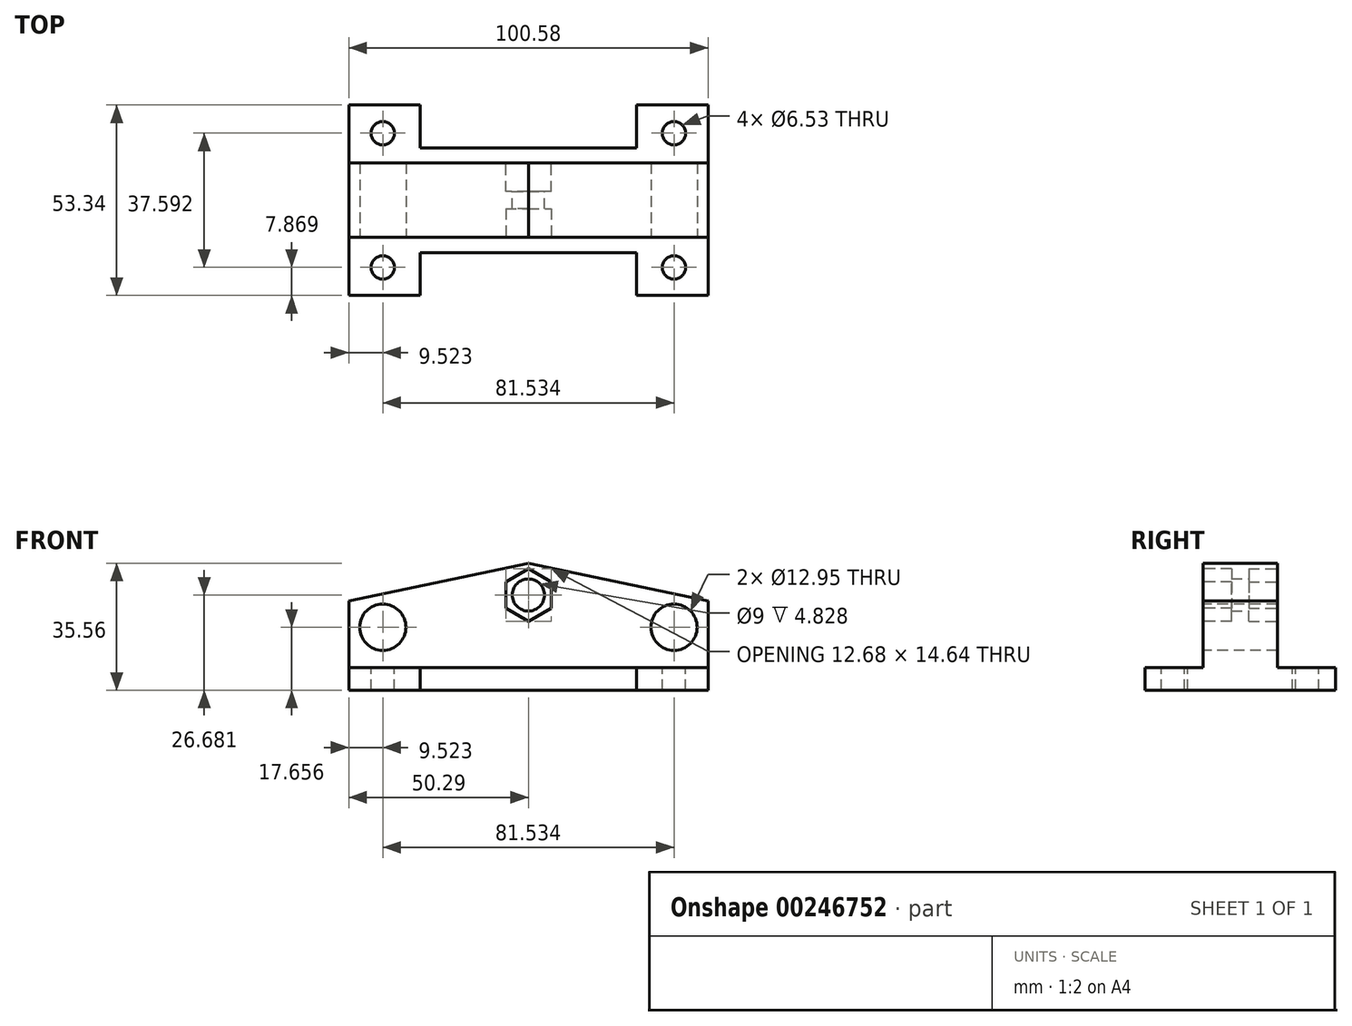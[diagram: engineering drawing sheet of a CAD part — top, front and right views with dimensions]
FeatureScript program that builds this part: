
annotation { "Feature Type Name" : "Feature", "Feature Type Description" : "" }
export const myFeature = defineFeature(function(context is Context, id is Id, definition is map)
    precondition{}
    {
        {
            var Q0;
            Q0=qCreatedBy(makeId("Top.planeOp"),FACE);
            var sketch = newSketch(context, id + "F0", { "sketchPlane" : qUnion([Q0])});
            skLineSegment(sketch, "E0.bottom", {"start": v(-48.14, 27.76) * mm, "end": v(52.44, 27.76) * mm});
            skLineSegment(sketch, "E0.top", {"start": v(-48.14, -25.58) * mm, "end": v(52.44, -25.58) * mm});
            skLineSegment(sketch, "E0.left", {"start": v(-48.14, 27.76) * mm, "end": v(-48.14, -25.58) * mm});
            skLineSegment(sketch, "E0.right", {"start": v(52.44, 27.76) * mm, "end": v(52.44, -25.58) * mm});
            skSolve(sketch);
        }
        {
            var Q0;
            Q0 = qSketchRegion(id + "F0", true);
            extrude(context, id + "F1", {"entities" : qUnion([Q0]), "depth" : 6.35 * mm});
        }
        {
            var Q0;
            Q0=makeQuery(id+"F1.opExtrude","CAP_FACE",FACE,{"disambiguationData":[OSD([sQuery(id+"F0.wireOp",EDGE,"E0.bottom"),sQuery(id+"F0.wireOp",EDGE,"E0.top"),sQuery(id+"F0.wireOp",EDGE,"E0.left"),sQuery(id+"F0.wireOp",EDGE,"E0.right")])],"isStart":false});
            var sketch = newSketch(context, id + "F2", { "sketchPlane" : qUnion([Q0])});
            skLineSegment(sketch, "E1.bottom", {"start": v(-48.14, 11.5) * mm, "end": v(52.44, 11.5) * mm});
            skLineSegment(sketch, "E1.top", {"start": v(-48.14, -9.33) * mm, "end": v(52.44, -9.33) * mm});
            skLineSegment(sketch, "E1.left", {"start": v(-48.14, 11.5) * mm, "end": v(-48.14, -9.33) * mm});
            skLineSegment(sketch, "E1.right", {"start": v(52.44, 11.5) * mm, "end": v(52.44, -9.33) * mm});
            skSolve(sketch);
        }
        {
            var Q0;
            Q0 = qSketchRegion(id + "F2", true);
            extrude(context, id + "F3", {"entities" : qUnion([Q0]), "operationType" : NewBodyOperationType.ADD, "depth" : 29.21 * mm});
        }
        {
            var Q0;
            Q0=makeQuery(id+"F3.opExtrude","SWEPT_FACE",FACE,{"disambiguationData":[OSD([sQuery(id+"F2.wireOp",EDGE,"E1.top")])]});
            var sketch = newSketch(context, id + "F4", { "sketchPlane" : qUnion([Q0])});
            skCircle(sketch, "E2.cCircle", {"center": v(2.15, 26.68) * mm, "radius": 6.34 * mm, "construction": true});
            skLineSegment(sketch, "E2.0", {"start": v(8.49, 30.34) * mm, "end": v(8.49, 23.02) * mm});
            skLineSegment(sketch, "E2.1", {"start": v(8.49, 23.02) * mm, "end": v(2.15, 19.36) * mm});
            skLineSegment(sketch, "E2.2", {"start": v(2.15, 19.36) * mm, "end": v(-4.2, 23.02) * mm});
            skLineSegment(sketch, "E2.3", {"start": v(-4.2, 23.02) * mm, "end": v(-4.2, 30.34) * mm});
            skLineSegment(sketch, "E2.4", {"start": v(-4.2, 30.34) * mm, "end": v(2.15, 34) * mm});
            skLineSegment(sketch, "E2.5", {"start": v(2.15, 34) * mm, "end": v(8.49, 30.34) * mm});
            skPoint(sketch, "E2.0.midPoint", {"position": v(8.49, 26.68) * mm});
            skSolve(sketch);
        }
        {
            var Q0;
            Q0 = qSketchRegion(id + "F4", true);
            extrude(context, id + "F5", {"entities" : qUnion([Q0]), "operationType" : NewBodyOperationType.REMOVE, "oppositeDirection" : true, "depth" : 8 * mm});
        }
        {
            var Q0;
            Q0=makeQuery(id+"F3.opExtrude","SWEPT_FACE",FACE,{"disambiguationData":[OSD([sQuery(id+"F2.wireOp",EDGE,"E1.bottom")])]});
            var sketch = newSketch(context, id + "F6", { "sketchPlane" : qUnion([Q0])});
            skCircle(sketch, "E3.cCircle", {"center": v(-2.15, 26.68) * mm, "radius": 6.34 * mm, "construction": true});
            skLineSegment(sketch, "E3.0", {"start": v(4.2, 30.34) * mm, "end": v(4.2, 23.02) * mm});
            skLineSegment(sketch, "E3.1", {"start": v(4.2, 23.02) * mm, "end": v(-2.15, 19.36) * mm});
            skLineSegment(sketch, "E3.2", {"start": v(-2.15, 19.36) * mm, "end": v(-8.49, 23.02) * mm});
            skLineSegment(sketch, "E3.3", {"start": v(-8.49, 23.02) * mm, "end": v(-8.49, 30.34) * mm});
            skLineSegment(sketch, "E3.4", {"start": v(-8.49, 30.34) * mm, "end": v(-2.15, 34) * mm});
            skLineSegment(sketch, "E3.5", {"start": v(-2.15, 34) * mm, "end": v(4.2, 30.34) * mm});
            skPoint(sketch, "E3.0.midPoint", {"position": v(4.2, 26.68) * mm});
            skSolve(sketch);
        }
        {
            var Q0;
            Q0 = qSketchRegion(id + "F6", true);
            extrude(context, id + "F7", {"entities" : qUnion([Q0]), "operationType" : NewBodyOperationType.REMOVE, "oppositeDirection" : true, "depth" : 8 * mm});
        }
        {
            var Q0;
            Q0=makeQuery(id+"F3.opExtrude","SWEPT_FACE",FACE,{"disambiguationData":[OSD([sQuery(id+"F2.wireOp",EDGE,"E1.bottom")])]});
            var sketch = newSketch(context, id + "F8", { "sketchPlane" : qUnion([Q0])});
            skPoint(sketch, "E4", {"position": v(-2.15, 26.68) * mm});
            skPoint(sketch, "E4.positionSnap0", {"position": v(4.2, 26.68) * mm});
            skSolve(sketch);
        }
        {
            var Q0;
            Q0=sQuery(id+"F8.wireOp",VERTEX,"E4");
            var Q1;
            Q1=makeQuery(id+"F1.opExtrude","SWEPT_BODY",BODY,{"disambiguationData":[OSD([sQuery(id+"F0.wireOp",EDGE,"E0.bottom"),sQuery(id+"F0.wireOp",EDGE,"E0.top"),sQuery(id+"F0.wireOp",EDGE,"E0.left"),sQuery(id+"F0.wireOp",EDGE,"E0.right")])]});
            hole(context, id + "F9", {"style" : HoleStyle.SIMPLE, "endStyle" : HoleEndStyle.THROUGH, "holeDiameter" : 9 * mm, "tappedDepth" : 12 * mm, "tapClearance" : 3, "locations" : qUnion([Q0]), "scope" : qUnion([Q1])});
        }
        {
            var Q0;
            Q0=makeQuery(id+"F3.opExtrude","SWEPT_FACE",FACE,{"disambiguationData":[OSD([sQuery(id+"F2.wireOp",EDGE,"E1.top")])]});
            var sketch = newSketch(context, id + "F10", { "sketchPlane" : qUnion([Q0])});
            skPoint(sketch, "E5", {"position": v(-38.62, 17.66) * mm});
            skPoint(sketch, "E6", {"position": v(42.92, 17.66) * mm});
            skSolve(sketch);
        }
        {
            var Q0;
            Q0=sQuery(id+"F10.wireOp",VERTEX,"E6");
            var Q1;
            Q1=sQuery(id+"F10.wireOp",VERTEX,"E5");
            var Q2;
            Q2=makeQuery(id+"F1.opExtrude","SWEPT_BODY",BODY,{"disambiguationData":[OSD([sQuery(id+"F0.wireOp",EDGE,"E0.bottom"),sQuery(id+"F0.wireOp",EDGE,"E0.top"),sQuery(id+"F0.wireOp",EDGE,"E0.left"),sQuery(id+"F0.wireOp",EDGE,"E0.right")])]});
            hole(context, id + "F11", {"style" : HoleStyle.SIMPLE, "endStyle" : HoleEndStyle.THROUGH, "holeDiameter" : 12.95 * mm, "tappedDepth" : 12 * mm, "tapClearance" : 3, "locations" : qUnion([Q0, Q1]), "scope" : qUnion([Q2])});
        }
        {
            var Q0;
            {var subQ0=sQuery(id+"F0.wireOp",EDGE,"E0.right");var subQ1=sQuery(id+"F0.wireOp",EDGE,"E0.left");var subQ2=sQuery(id+"F0.wireOp",EDGE,"E0.top");Q0=makeQuery(id+"F3.boolean.opBoolean","SPLIT",FACE,{"disambiguationData":[TD([makeQuery(id+"F1.opExtrude","SWEPT_FACE",FACE,{"disambiguationData":[OSD([subQ2])]})])],"derivedFrom":makeQuery(id+"F1.opExtrude","CAP_FACE",FACE,{"disambiguationData":[OSD([sQuery(id+"F0.wireOp",EDGE,"E0.bottom"),subQ2,subQ1,subQ0])],"isStart":false})});}
            var sketch = newSketch(context, id + "F12", { "sketchPlane" : qUnion([Q0])});
            skPoint(sketch, "E7", {"position": v(-38.62, -17.71) * mm});
            skPoint(sketch, "E8", {"position": v(42.92, -17.71) * mm});
            skPoint(sketch, "E9", {"position": v(42.92, 19.88) * mm});
            skPoint(sketch, "E10", {"position": v(-38.62, 19.88) * mm});
            skSolve(sketch);
        }
        {
            var Q0;
            Q0=sQuery(id+"F12.wireOp",VERTEX,"E7");
            var Q1;
            Q1=sQuery(id+"F12.wireOp",VERTEX,"E10");
            var Q2;
            Q2=sQuery(id+"F12.wireOp",VERTEX,"E9");
            var Q3;
            Q3=sQuery(id+"F12.wireOp",VERTEX,"E8");
            var Q4;
            Q4=makeQuery(id+"F1.opExtrude","SWEPT_BODY",BODY,{"disambiguationData":[OSD([sQuery(id+"F0.wireOp",EDGE,"E0.bottom"),sQuery(id+"F0.wireOp",EDGE,"E0.top"),sQuery(id+"F0.wireOp",EDGE,"E0.left"),sQuery(id+"F0.wireOp",EDGE,"E0.right")])]});
            hole(context, id + "F13", {"style" : HoleStyle.SIMPLE, "endStyle" : HoleEndStyle.THROUGH, "holeDiameter" : 6.53 * mm, "tappedDepth" : 12 * mm, "tapClearance" : 3, "locations" : qUnion([Q0, Q1, Q2, Q3]), "scope" : qUnion([Q4])});
        }
        {
            var Q0;
            {var subQ0=sQuery(id+"F0.wireOp",EDGE,"E0.right");var subQ1=sQuery(id+"F0.wireOp",EDGE,"E0.left");var subQ2=sQuery(id+"F0.wireOp",EDGE,"E0.bottom");Q0=makeQuery(id+"F3.boolean.opBoolean","SPLIT",FACE,{"disambiguationData":[TD([makeQuery(id+"F1.opExtrude","SWEPT_FACE",FACE,{"disambiguationData":[OSD([subQ2])]})])],"derivedFrom":makeQuery(id+"F1.opExtrude","CAP_FACE",FACE,{"disambiguationData":[OSD([subQ2,sQuery(id+"F0.wireOp",EDGE,"E0.top"),subQ1,subQ0])],"isStart":false})});}
            var sketch = newSketch(context, id + "F14", { "sketchPlane" : qUnion([Q0])});
            skLineSegment(sketch, "E11.bottom", {"start": v(-28.14, 27.76) * mm, "end": v(32.44, 27.76) * mm});
            skLineSegment(sketch, "E11.top", {"start": v(-28.14, 15.76) * mm, "end": v(32.44, 15.76) * mm});
            skLineSegment(sketch, "E11.left", {"start": v(-28.14, 27.76) * mm, "end": v(-28.14, 15.76) * mm});
            skLineSegment(sketch, "E11.right", {"start": v(32.44, 27.76) * mm, "end": v(32.44, 15.76) * mm});
            skSolve(sketch);
        }
        {
            var Q0;
            Q0=makeQuery(id+"F14.imprint","IMPRINT",FACE,{"disambiguationData":[TD([[makeQuery(id+"F14.imprint","IMPRINT",EDGE,{"derivedFrom":sQuery(id+"F14.wireOp",EDGE,"E11.bottom")}),-1.0]])]});
            extrude(context, id + "F15", {"entities" : qUnion([Q0]), "operationType" : NewBodyOperationType.REMOVE, "endBound" : BoundingType.UP_TO_NEXT, "oppositeDirection" : true, "depth" : 25 * mm});
        }
        {
            var Q0;
            {var subQ0=sQuery(id+"F0.wireOp",EDGE,"E0.right");var subQ1=sQuery(id+"F0.wireOp",EDGE,"E0.left");var subQ2=sQuery(id+"F0.wireOp",EDGE,"E0.top");Q0=makeQuery(id+"F3.boolean.opBoolean","SPLIT",FACE,{"disambiguationData":[TD([makeQuery(id+"F1.opExtrude","SWEPT_FACE",FACE,{"disambiguationData":[OSD([subQ2])]})])],"derivedFrom":makeQuery(id+"F1.opExtrude","CAP_FACE",FACE,{"disambiguationData":[OSD([sQuery(id+"F0.wireOp",EDGE,"E0.bottom"),subQ2,subQ1,subQ0])],"isStart":false})});}
            var sketch = newSketch(context, id + "F16", { "sketchPlane" : qUnion([Q0])});
            skLineSegment(sketch, "E12.bottom", {"start": v(-28.14, -25.58) * mm, "end": v(32.44, -25.58) * mm});
            skLineSegment(sketch, "E12.top", {"start": v(-28.14, -13.58) * mm, "end": v(32.44, -13.58) * mm});
            skLineSegment(sketch, "E12.left", {"start": v(-28.14, -25.58) * mm, "end": v(-28.14, -13.58) * mm});
            skLineSegment(sketch, "E12.right", {"start": v(32.44, -25.58) * mm, "end": v(32.44, -13.58) * mm});
            skSolve(sketch);
        }
        {
            var Q0;
            Q0 = qSketchRegion(id + "F16", true);
            extrude(context, id + "F17", {"entities" : qUnion([Q0]), "operationType" : NewBodyOperationType.REMOVE, "endBound" : BoundingType.UP_TO_NEXT, "oppositeDirection" : true, "depth" : 25 * mm});
        }
        {
            var Q0;
            Q0=makeQuery(id+"F3.opExtrude","SWEPT_FACE",FACE,{"disambiguationData":[OSD([sQuery(id+"F2.wireOp",EDGE,"E1.top")])]});
            var sketch = newSketch(context, id + "F18", { "sketchPlane" : qUnion([Q0])});
            skLineSegment(sketch, "E13", {"start": v(2.15, 35.56) * mm, "end": v(52.44, 25.01) * mm});
            skLineSegment(sketch, "E14", {"start": v(52.44, 25.01) * mm, "end": v(52.44, 35.56) * mm});
            skLineSegment(sketch, "E15", {"start": v(52.44, 35.56) * mm, "end": v(2.15, 35.56) * mm});
            skLineSegment(sketch, "E16", {"start": v(2.15, 35.56) * mm, "end": v(-48.14, 25.01) * mm});
            skLineSegment(sketch, "E17", {"start": v(-48.14, 25.01) * mm, "end": v(-48.14, 35.56) * mm});
            skLineSegment(sketch, "E18", {"start": v(-48.14, 35.56) * mm, "end": v(2.15, 35.56) * mm});
            skSolve(sketch);
        }
        {
            var Q0;
            Q0=makeQuery(id+"F18.imprint","IMPRINT",FACE,{"disambiguationData":[TD([[makeQuery(id+"F18.imprint","IMPRINT",EDGE,{"derivedFrom":sQuery(id+"F18.wireOp",EDGE,"E16")}),-1.0]])]});
            var Q1;
            Q1=makeQuery(id+"F18.imprint","IMPRINT",FACE,{"disambiguationData":[TD([[makeQuery(id+"F18.imprint","IMPRINT",EDGE,{"derivedFrom":sQuery(id+"F18.wireOp",EDGE,"E13")}),1.0]])]});
            extrude(context, id + "F19", {"entities" : qUnion([Q0, Q1]), "operationType" : NewBodyOperationType.REMOVE, "endBound" : BoundingType.UP_TO_NEXT, "oppositeDirection" : true, "depth" : 25 * mm});
        }
    });
